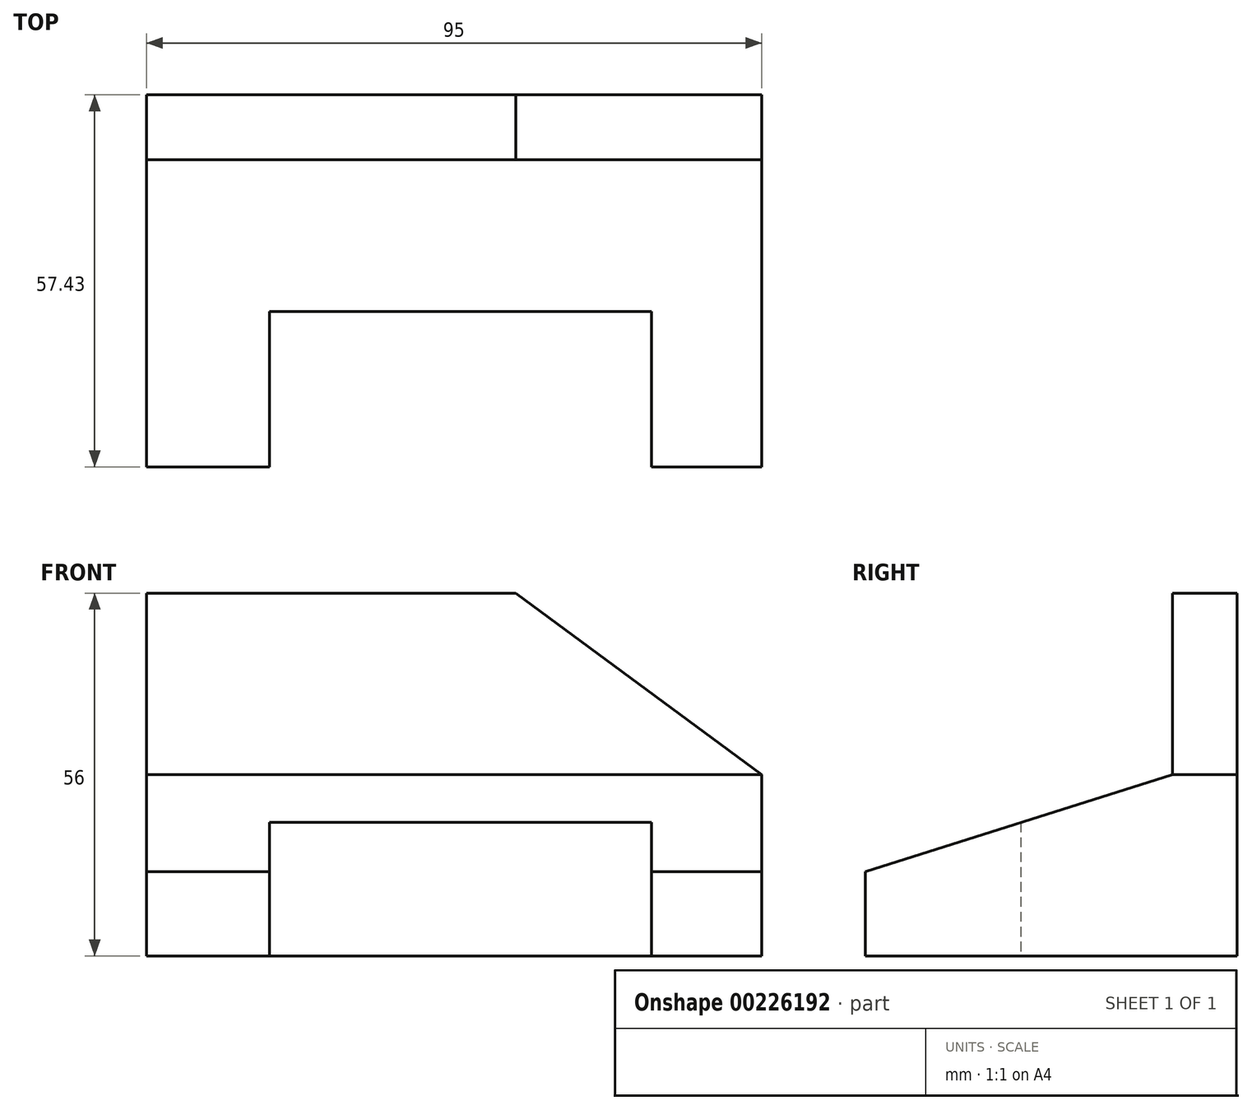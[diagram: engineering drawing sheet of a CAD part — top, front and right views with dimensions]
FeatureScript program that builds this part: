
annotation { "Feature Type Name" : "Feature", "Feature Type Description" : "" }
export const myFeature = defineFeature(function(context is Context, id is Id, definition is map)
    precondition{}
    {
        {
            var Q0;
            Q0=qCreatedBy(makeId("Right.planeOp"),FACE);
            var sketch = newSketch(context, id + "F0", { "sketchPlane" : qUnion([Q0])});
            skLineSegment(sketch, "E0", {"start": v(0, 0) * mm, "end": v(0, 56) * mm});
            skLineSegment(sketch, "E1", {"start": v(0, 56) * mm, "end": v(-10, 56) * mm});
            skLineSegment(sketch, "E2", {"start": v(-10, 56) * mm, "end": v(-10, 28) * mm});
            skLineSegment(sketch, "E3", {"start": v(-10, 28) * mm, "end": v(0, 28) * mm});
            skLineSegment(sketch, "E4", {"start": v(0, 0) * mm, "end": v(-57.43, 0) * mm});
            skLineSegment(sketch, "E5", {"start": v(-57.43, 0) * mm, "end": v(-57.43, 13) * mm});
            skLineSegment(sketch, "E6", {"start": v(-57.43, 13) * mm, "end": v(-10, 28) * mm});
            skSolve(sketch);
        }
        {
            var Q0;
            {var subQ1=sQuery(id+"F0.wireOp",EDGE,"E3");Q0=makeQuery(id+"F0.imprint","IMPRINT",FACE,{"disambiguationData":[TD([[makeQuery(id+"F0.imprint","IMPRINT",EDGE,{"derivedFrom":subQ1}),-1.0]])]});}
            var Q1;
            {var subQ0=sQuery(id+"F0.wireOp",EDGE,"E1");Q1=makeQuery(id+"F0.imprint","IMPRINT",FACE,{"disambiguationData":[TD([[makeQuery(id+"F0.imprint","IMPRINT",EDGE,{"derivedFrom":subQ0}),1.0]])]});}
            extrude(context, id + "F1", {"entities" : qUnion([Q0, Q1]), "oppositeDirection" : true, "depth" : 95 * mm});
        }
        {
            var Q0;
            Q0=makeQuery(id+"F1.opExtrude","SWEPT_FACE",FACE,{"disambiguationData":[OSD([sQuery(id+"F0.wireOp",EDGE,"E2")])]});
            var sketch = newSketch(context, id + "F2", { "sketchPlane" : qUnion([Q0])});
            skLineSegment(sketch, "E7", {"start": v(-38, 56) * mm, "end": v(0, 28) * mm});
            skLineSegment(sketch, "E8", {"start": v(-38, 56) * mm, "end": v(0, 56) * mm});
            skLineSegment(sketch, "E9", {"start": v(0, 56) * mm, "end": v(0, 28) * mm});
            skSolve(sketch);
        }
        {
            var Q0;
            Q0=makeQuery(id+"F2.imprint","IMPRINT",FACE,{"disambiguationData":[TD([[makeQuery(id+"F2.imprint","IMPRINT",EDGE,{"derivedFrom":sQuery(id+"F2.wireOp",EDGE,"E7")}),1.0]])]});
            extrude(context, id + "F3", {"entities" : qUnion([Q0]), "operationType" : NewBodyOperationType.REMOVE, "oppositeDirection" : true, "depth" : 10 * mm});
        }
        {
            var Q0;
            Q0=makeQuery(id+"F1.opExtrude","SWEPT_FACE",FACE,{"disambiguationData":[OSD([sQuery(id+"F0.wireOp",EDGE,"E4")])]});
            var sketch = newSketch(context, id + "F4", { "sketchPlane" : qUnion([Q0])});
            skLineSegment(sketch, "E10", {"start": v(-76, 57.43) * mm, "end": v(-76, 33.43) * mm});
            skLineSegment(sketch, "E11", {"start": v(-76, 33.43) * mm, "end": v(-17, 33.43) * mm});
            skLineSegment(sketch, "E12", {"start": v(-17, 33.43) * mm, "end": v(-17, 57.43) * mm});
            skLineSegment(sketch, "E13", {"start": v(-17, 57.43) * mm, "end": v(-76, 57.43) * mm});
            skSolve(sketch);
        }
        {
            var Q0;
            Q0=makeQuery(id+"F4.imprint","IMPRINT",FACE,{"disambiguationData":[TD([[makeQuery(id+"F4.imprint","IMPRINT",EDGE,{"derivedFrom":sQuery(id+"F4.wireOp",EDGE,"E10")}),1.0]])]});
            extrude(context, id + "F5", {"entities" : qUnion([Q0]), "operationType" : NewBodyOperationType.REMOVE, "oppositeDirection" : true, "depth" : 62.4 * mm});
        }
    });
